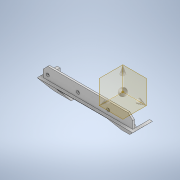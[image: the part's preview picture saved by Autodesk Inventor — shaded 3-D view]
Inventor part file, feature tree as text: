
AUTODESK INVENTOR PART (.ipt)
format: ipt  version: 2021 (Build 250183000, 183)  size: 668,160 bytes
history: native  units: mm
features: sketch x33, extrude x31, chamfer x11, fillet x5, hole x2
ambient origin geometry x8: Origin, YZ Plane, XZ Plane, XY Plane, X Axis, Y Axis, Z Axis, Center Point
bodies: Solid1 (feature_tree)
feature tree (82):
  extrude  "Extrusion1"  Depth=100.0mm
  extrude  "Extrusion3"  Depth=50.0mm
  extrude  "Extrusion4"  Depth=12.5mm
  extrude  "Extrusion12"  Depth=3.0mm TaperAngle=0.0deg
  extrude  "Extrusion13"  Depth=3.0mm TaperAngle=0.0deg
  fillet  "Fillet3"  Radius=2.0mm
  extrude  "Extrusion15"  Depth=2.0mm
  extrude  "Extrusion20"  Depth=1.2mm
  extrude  "Extrusion21"  Depth=12.0mm TaperAngle=0.0deg
  extrude  "Extrusion22"  Depth=2.0mm
  extrude  "Extrusion23"  Depth=3.0mm
  extrude  "Extrusion26"  Depth=4.4mm TaperAngle=0.0deg
  hole  "Hole2"  [1 undecoded]
  chamfer  "Chamfer3"  Distance=12.0mm
  chamfer  "Chamfer4"  Distance=12.0mm
  chamfer  "Chamfer5"  Distance=2.0mm
  chamfer  "Chamfer6"  Distance=2.0mm
  chamfer  "Chamfer7"  Distance=4.8mm
  extrude  "Extrusion27"  Depth=0.5mm
  fillet  "Fillet4"  Radius=4.8mm
  extrude  "Extrusion28"  Depth=0.5mm
  extrude  "Extrusion29"  Depth=5.0mm TaperAngle=0.0deg
  extrude  "Extrusion30"  Depth=2.0mm TaperAngle=45.0deg
  fillet  "Fillet5"  Radius=1.0mm
  extrude  "Extrusion34"  Depth=2.0mm TaperAngle=45.0deg
  extrude  "Extrusion35"  Depth=2.0mm TaperAngle=45.0deg
  extrude  "Extrusion36"  Depth=0.8mm TaperAngle=45.0deg
  extrude  "Extrusion37"  Depth=0.5mm
  fillet  "Fillet6"  Radius=2.0mm
  extrude  "Extrusion38"  Depth=2.0mm
  extrude  "Extrusion39"  Depth=2.0mm
  chamfer  "Chamfer8"  Distance=24.0mm
  extrude  "Extrusion40"  Depth=2.0mm TaperAngle=0.0deg
  fillet  "Fillet7"  Radius=36.5mm
  extrude  "Extrusion41"  Depth=0.5mm
  chamfer  "Chamfer9"  Distance=3.5mm
  extrude  "Extrusion42"  Depth=2.0mm TaperAngle=0.0deg
  extrude  "Extrusion43"  Depth=12.5mm
  extrude  "Extrusion44"  Depth=0.5mm
  extrude  "Extrusion45"  Depth=0.5mm
  hole  "Hole3"  [1 undecoded]
  extrude  "Extrusion46"  Depth=1.0mm
  extrude  "Extrusion47"  Depth=7.6mm
  chamfer  "Chamfer10"  Distance=10.0mm
  extrude  "Extrusion48"  Depth=46.4mm
  chamfer  "Chamfer11"  Distance=20.0mm
  extrude  "Extrusion49"  Depth=0.5mm
  chamfer  "Chamfer12"  Distance=67.0mm
  chamfer  "Chamfer13"  Distance=1.2mm
  sketch  "Sketch1"  dims[d0=52.0mm d1=100.0mm]
  sketch  "Sketch4"  dims[d2=26.0mm d3=50.0mm]
  sketch  "Sketch5"  dims[d4=1.2mm d5=0.0mm d35=12.5mm]
  sketch  "Sketch13"  dims[d36=63.1mm d37=3.0mm d38=0.0mm]
  sketch  "Sketch14"  dims[d39=50.673mm d40=3.0mm d41=0.0mm d79=2.0mm]
  sketch  "Sketch16"  dims[d80=2.0mm d81=2.0mm]
  sketch  "Sketch21"  dims[d82=1.2mm d83=44.0mm]
  sketch  "Sketch22"  dims[d84=59.0mm d85=12.0mm d86=0.0mm]
  sketch  "Sketch23"  dims[d87=2.0mm d88=12.6mm]
  sketch  "Sketch24"  dims[d89=12.0mm d90=0.0mm d91=3.0mm]
  sketch  "Sketch27"  dims[d95=33.8mm d96=4.4mm d97=0.0mm]
  sketch  "Sketch28"  dims[d117=2.0mm d118=2.0mm d119=12.0mm d120=0.0mm d121=12.0mm d122=0.0mm]
  sketch  "Sketch29"  dims[d123=70.0mm]
  sketch  "Sketch30"  dims[d124=89.0mm]
  sketch  "Sketch31"  dims[d125=8.0mm]
  sketch  "Sketch32"  dims[d126=8.0mm d127=2.0mm d128=0.0mm]
  sketch  "Sketch36"  dims[d129=8.0mm]
  sketch  "Sketch37"  dims[d130=10.0mm]
  sketch  "Sketch38"  dims[d131=12.0mm]
  sketch  "Sketch39"  dims[d132=8.0mm]
  sketch  "Sketch40"  dims[d133=8.0mm]
  sketch  "Sketch41"  dims[d134=8.0mm d135=2.0mm d136=0.0mm]
  sketch  "Sketch43"  dims[d144=3.0mm]
  sketch  "Sketch45"  dims[d145=3.0mm]
  sketch  "Sketch46"  dims[d146=3.0mm]
  sketch  "Sketch47"  dims[d147=50.0mm]
  sketch  "Sketch48"  dims[d148=97.0mm]
  sketch  "Sketch49"  dims[d149=15.0mm]
  sketch  "Sketch50"  dims[d150=3.0mm]
  sketch  "Sketch51"  dims[d151=3.0mm]
  sketch  "Sketch52"  dims[d152=97.0mm]
  sketch  "Sketch53"  dims[d153=49.0mm]
  sketch  "Sketch54"  dims[d154=4.8mm d155=4.8mm d156=4.8mm d157=4.8mm d158=4.8mm d159=5.0mm d160=0.0mm d161=2.0mm d162=6.0mm d163=4.0mm d164=2.0mm d165=90.0deg d166=4.0mm d167=20.594885mm d168=2.0mm d169=2.0mm d170=45.0deg d171=1.0mm d172=2.0mm d173=45.0deg d174=2.0mm d175=2.0mm d176=45.0deg d177=2.0mm d178=2.0mm d179=45.0deg d180=0.8mm d181=2.0mm d182=45.0deg d184=68.0mm d189=2.0mm d190=0.0mm d191=2.0mm d192=2.0mm d193=24.0mm d194=2.0mm d195=0.0mm d196=36.5mm d197=46.5mm d198=3.5mm d199=2.0mm d200=0.0mm d201=12.5mm d202=23.0mm d203=3.5mm d204=2.0mm d205=0.0mm d206=1.0mm d217=7.6mm d218=10.0mm d219=46.4mm d220=20.0mm d221=0.0mm d222=22.68928mm d223=67.0mm d224=0.0mm d225=1.2mm d226=0.0mm d227=1.2mm d228=0.0mm d229=3.0mm d230=12.3mm d231=33.2mm d232=1.0mm d233=10.0mm d234=1.2mm d235=0.0mm d236=1.2mm d237=5.0mm d238=20.0mm d239=1.5mm d240=0.0mm d241=1.5mm d242=2.0mm d243=45.0deg d245=2.711255mm d246=12.0mm d247=33.2mm d248=3.0mm d249=0.0mm d251=2.0mm d252=1.2mm d253=10.0mm d254=1.5mm d255=0.0mm d256=1.5mm d257=2.0mm d258=45.0deg d259=50.0mm d260=0.0mm d261=1.6mm d262=1.6mm d263=8.0mm d264=0.0mm d265=2.0mm d266=0.0mm d267=1.6mm d268=5.0mm d269=0.0mm d270=20.0mm d271=20.0mm d272=5.0mm d273=3.1mm d274=3.1mm d275=3.1mm d276=2.0mm d277=6.0mm d278=4.0mm d279=2.0mm d280=90.0deg d281=4.0mm d282=20.594885mm d283=2.0mm d284=0.0mm d285=5.0mm d286=2.0mm d287=0.0mm d288=1.6mm d289=2.0mm d290=45.0deg d291=2.0mm d292=0.0mm d293=3.0mm d294=2.0mm d295=45.0deg d296=3.0mm d297=0.0mm d298=0.85mm d299=2.0mm d300=45.0deg d301=1.2mm d302=2.0mm d303=45.0deg d67=0.5mm d68=0.872665mm d69=0.5mm d70=0.872665mm d71=0.5mm d72=0.872665mm d73=0.5mm d74=0.872665mm d75=0.872665mm d76=0.5mm d77=0.872665mm d208=0.5mm d209=0.872665mm d210=0.5mm d211=0.872665mm]
note: 2 required parameter values undecoded (feature->parameter linkage not recoverable at this tier; creation-order binding heuristic only, values carry confidence <= 0.55)
